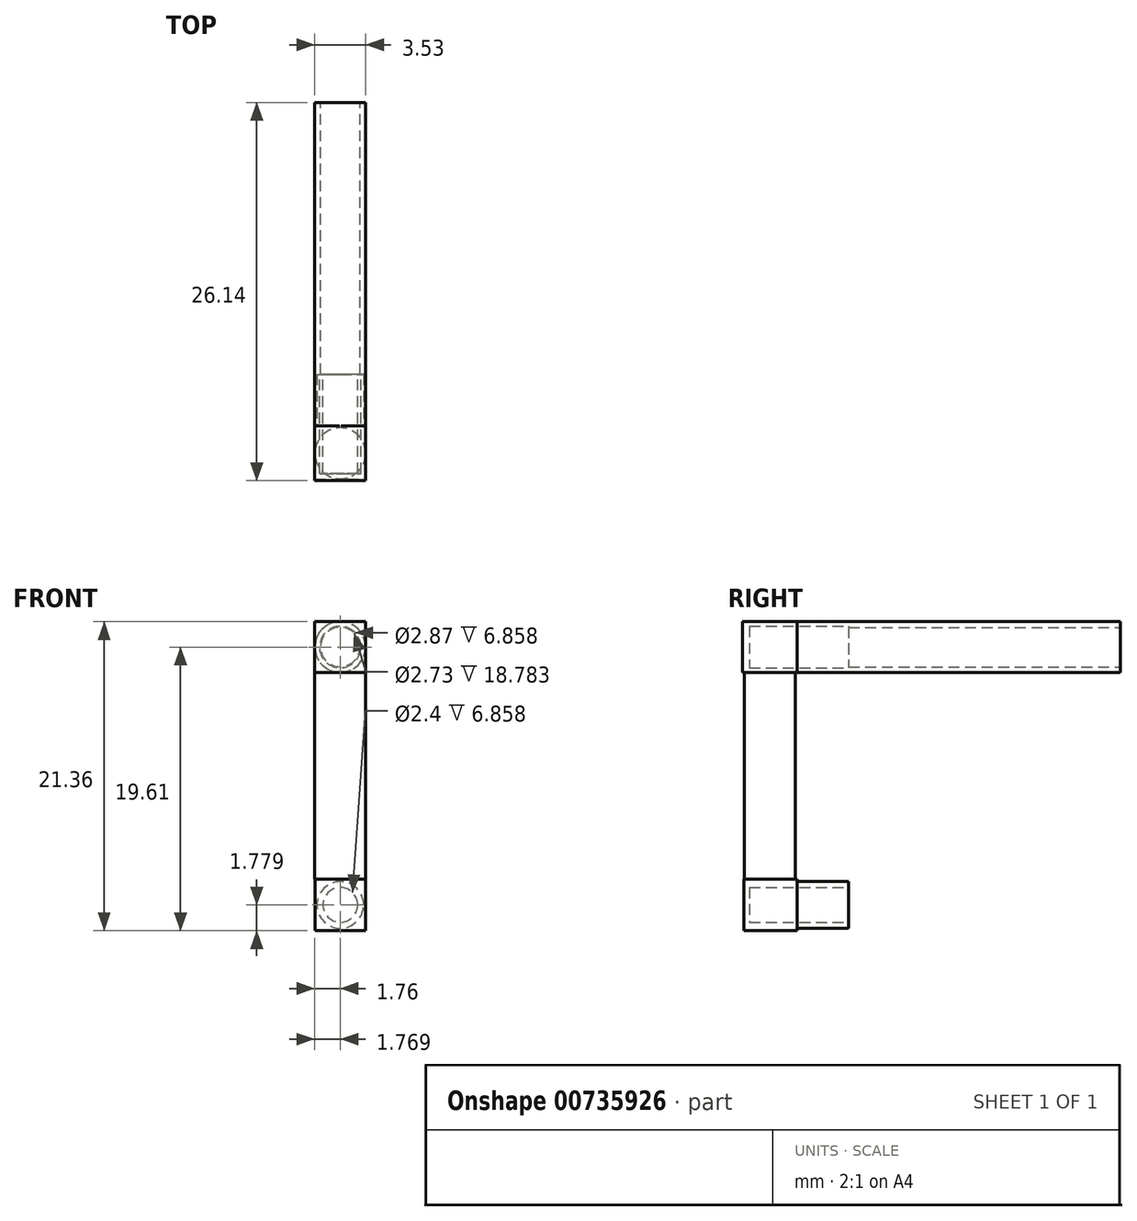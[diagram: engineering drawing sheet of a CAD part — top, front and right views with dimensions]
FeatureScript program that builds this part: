
annotation { "Feature Type Name" : "Feature", "Feature Type Description" : "" }
export const myFeature = defineFeature(function(context is Context, id is Id, definition is map)
    precondition{}
    {
        {
            var Q0;
            Q0=qCreatedBy(makeId("Front.planeOp"),FACE);
            var sketch = newSketch(context, id + "F0", { "sketchPlane" : qUnion([Q0])});
            skCircle(sketch, "E0", {"center": v(0, 0) * mm, "radius": 1.75 * mm});
            skSolve(sketch);
        }
        {
            var Q0;
            Q0 = qSketchRegion(id + "F0", true);
            extrude(context, id + "F1", {"entities" : qUnion([Q0]), "depth" : 22.35 * mm, "offsetDistance" : 25.4 * mm});
        }
        {
            var Q0;
            Q0=makeQuery(id+"F1.opExtrude","CAP_FACE",FACE,{"disambiguationData":[OSD([sQuery(id+"F0.wireOp",EDGE,"E0")])],"isStart":false});
            var sketch = newSketch(context, id + "F2", { "sketchPlane" : qUnion([Q0])});
            skLineSegment(sketch, "E1.bottom", {"start": v(-1.76, -1.75) * mm, "end": v(1.76, -1.75) * mm});
            skLineSegment(sketch, "E1.top", {"start": v(-1.76, 1.75) * mm, "end": v(1.76, 1.75) * mm});
            skLineSegment(sketch, "E1.left", {"start": v(-1.76, -1.75) * mm, "end": v(-1.76, 1.75) * mm});
            skLineSegment(sketch, "E1.right", {"start": v(1.76, -1.75) * mm, "end": v(1.76, 1.75) * mm});
            skSolve(sketch);
        }
        {
            var Q0;
            Q0 = qSketchRegion(id + "F2", true);
            extrude(context, id + "F3", {"entities" : qUnion([Q0]), "operationType" : NewBodyOperationType.ADD, "depth" : 3.78 * mm, "offsetDistance" : 25.4 * mm});
        }
        {
            var Q0;
            Q0=makeQuery(id+"F3.opExtrude","SWEPT_FACE",FACE,{"disambiguationData":[OSD([sQuery(id+"F2.wireOp",EDGE,"E1.bottom")])]});
            var sketch = newSketch(context, id + "F4", { "sketchPlane" : qUnion([Q0])});
            skCircle(sketch, "E2", {"center": v(0, 24.24) * mm, "radius": 1.76 * mm});
            skPoint(sketch, "E2.centerSnap0", {"position": v(-1.76, 24.24) * mm});
            skPoint(sketch, "E2.centerSnap1", {"position": v(0, 26.14) * mm});
            skSolve(sketch);
        }
        {
            var Q0;
            Q0 = qSketchRegion(id + "F4", true);
            extrude(context, id + "F5", {"entities" : qUnion([Q0]), "operationType" : NewBodyOperationType.ADD, "depth" : 14.3 * mm, "offsetDistance" : 25.4 * mm});
        }
        {
            var Q0;
            Q0=makeQuery(id+"F5.opExtrude","CAP_FACE",FACE,{"disambiguationData":[OSD([sQuery(id+"F4.wireOp",EDGE,"E2")])],"isStart":false});
            var sketch = newSketch(context, id + "F6", { "sketchPlane" : qUnion([Q0])});
            skLineSegment(sketch, "E3.bottom", {"start": v(-1.75, 26.03) * mm, "end": v(1.77, 26.03) * mm});
            skLineSegment(sketch, "E3.top", {"start": v(-1.75, 22.34) * mm, "end": v(1.77, 22.34) * mm});
            skLineSegment(sketch, "E3.left", {"start": v(-1.75, 26.03) * mm, "end": v(-1.75, 22.34) * mm});
            skLineSegment(sketch, "E3.right", {"start": v(1.77, 26.03) * mm, "end": v(1.77, 22.34) * mm});
            skSolve(sketch);
        }
        {
            var Q0;
            Q0 = qSketchRegion(id + "F6", true);
            extrude(context, id + "F7", {"entities" : qUnion([Q0]), "operationType" : NewBodyOperationType.ADD, "depth" : 3.56 * mm, "offsetDistance" : 25.4 * mm});
        }
        {
            var Q0;
            Q0=makeQuery(id+"F7.opExtrude","SWEPT_FACE",FACE,{"disambiguationData":[OSD([sQuery(id+"F6.wireOp",EDGE,"E3.top")])]});
            var sketch = newSketch(context, id + "F8", { "sketchPlane" : qUnion([Q0])});
            skCircle(sketch, "E4", {"center": v(0, -17.83) * mm, "radius": 1.61 * mm});
            skPoint(sketch, "E4.centerSnap0", {"position": v(0, -19.6) * mm});
            skPoint(sketch, "E4.centerSnap1", {"position": v(-1.77, -17.83) * mm});
            skSolve(sketch);
        }
        {
            var Q0;
            Q0 = qSketchRegion(id + "F8", true);
            extrude(context, id + "F9", {"entities" : qUnion([Q0]), "operationType" : NewBodyOperationType.ADD, "depth" : 3.56 * mm, "offsetDistance" : 25.4 * mm});
        }
        {
            var Q0;
            Q0=makeQuery(id+"F9.opExtrude","CAP_FACE",FACE,{"disambiguationData":[OSD([sQuery(id+"F8.wireOp",EDGE,"E4")])],"isStart":false});
            var sketch = newSketch(context, id + "F10", { "sketchPlane" : qUnion([Q0])});
            skCircle(sketch, "E5", {"center": v(0, 0) * mm, "radius": 1.43 * mm});
            skCircle(sketch, "E6", {"center": v(0, -17.83) * mm, "radius": 1.2 * mm});
            skSolve(sketch);
        }
        {
            var Q0;
            Q0 = qSketchRegion(id + "F10", true);
            extrude(context, id + "F11", {"entities" : qUnion([Q0]), "operationType" : NewBodyOperationType.REMOVE, "oppositeDirection" : true, "depth" : 6.86 * mm, "offsetDistance" : 25.4 * mm});
        }
        {
            var Q0;
            Q0=makeQuery(id+"F1.opExtrude","CAP_FACE",FACE,{"disambiguationData":[OSD([sQuery(id+"F0.wireOp",EDGE,"E0")])],"isStart":true});
            var sketch = newSketch(context, id + "F12", { "sketchPlane" : qUnion([Q0])});
            skCircle(sketch, "E7", {"center": v(0, 0) * mm, "radius": 1.36 * mm});
            skSolve(sketch);
        }
        {
            var Q0;
            Q0 = qSketchRegion(id + "F12", true);
            extrude(context, id + "F13", {"entities" : qUnion([Q0]), "operationType" : NewBodyOperationType.REMOVE, "oppositeDirection" : true, "depth" : 25.4 * mm, "offsetDistance" : 25.4 * mm});
        }
    });
